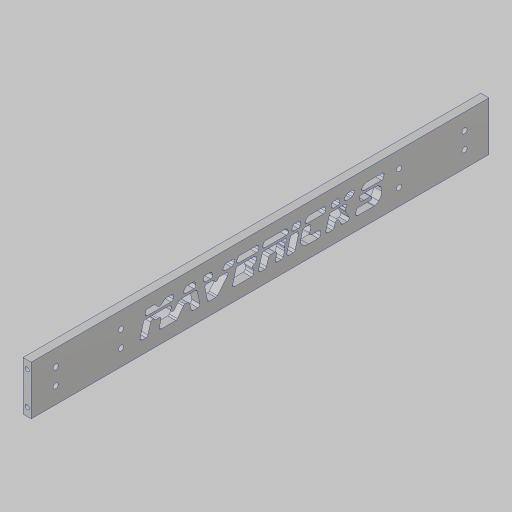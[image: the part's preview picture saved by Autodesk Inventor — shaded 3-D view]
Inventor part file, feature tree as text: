
AUTODESK INVENTOR PART (.ipt)
format: ipt  version: 2023.5 (Build 275446000, 446)  size: 567,808 bytes
history: native  units: in
note: dims shown in document units (in); Inventor stores cm internally (conversion verified against a paired STEP export)
features: sketch x4, hole x2, mirror x2, extrude x1, emboss x1, fillet x1
ambient origin geometry x8: Origin, YZ Plane, XZ Plane, XY Plane, X Axis, Y Axis, Z Axis, Center Point
bodies: Solid1 (feature_tree)
feature tree (11):
  extrude  "Extrusion1"  Depth=14.0in
  hole  "Hole2"  [1 undecoded]
  mirror  "Mirror1"
  hole  "Hole3"  [1 undecoded]
  mirror  "Mirror2"
  emboss  "Emboss1"
  fillet  "Fillet1"  Radius=0.5in
  sketch  "Sketch1"  dims[d1=1.5in d2=14.0in]
  sketch  "Sketch3"  dims[d3=0.25in d4=0.0in d20=0.25in]
  sketch  "Sketch4"  dims[d21=0.25in]
  sketch  "Sketch5"  dims[d22=0.13in d23=0.328in d24=0.332in d25=0.25in d26=0.5635in d27=0.5in d28=0.8108in d29=2.0in d30=0.5in d31=1.748in d32=0.156in d33=0.38in d34=0.385in d35=0.25in d36=0.5635in d37=1.0in d38=0.8108in d39=0.25in d40=0.0in d41=0.0625in]
note: 2 required parameter values undecoded (feature->parameter linkage not recoverable at this tier; creation-order binding heuristic only, values carry confidence <= 0.55)
